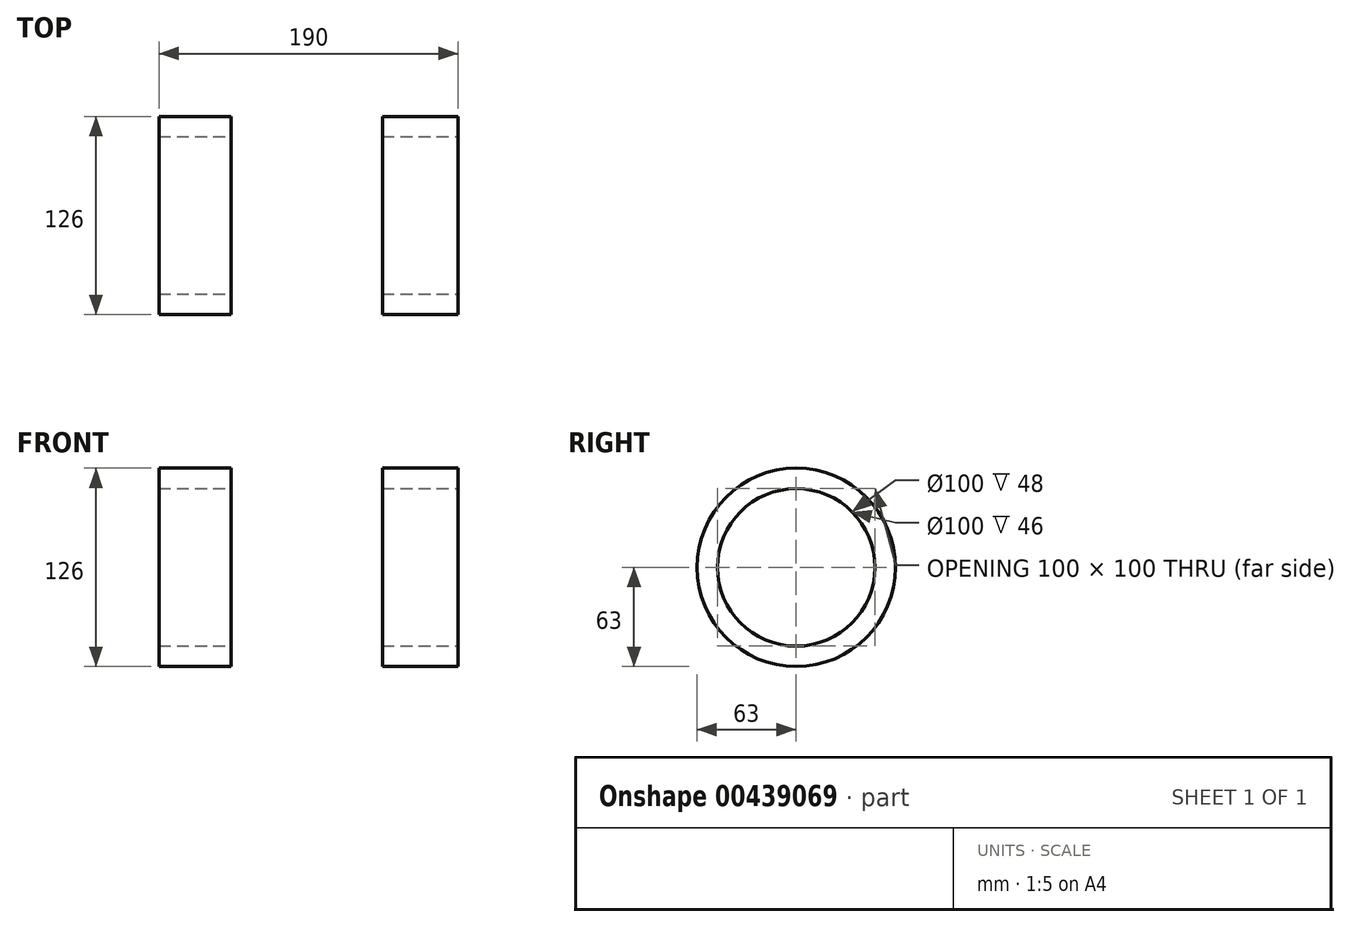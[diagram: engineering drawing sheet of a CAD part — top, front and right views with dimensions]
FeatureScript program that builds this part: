
annotation { "Feature Type Name" : "Feature", "Feature Type Description" : "" }
export const myFeature = defineFeature(function(context is Context, id is Id, definition is map)
    precondition{}
    {
        {
            var Q0;
            Q0=qCreatedBy(makeId("Right.planeOp"),FACE);
            var sketch = newSketch(context, id + "F0", { "sketchPlane" : qUnion([Q0])});
            skCircle(sketch, "E0", {"center": v(0, 0) * mm, "radius": 63 * mm});
            skSolve(sketch);
        }
        {
            var Q0;
            Q0=qSketchRegion(id+"F0",true);
            extrude(context, id + "F1", {"entities" : qUnion([Q0]), "depth" : 190 * mm});
        }
        {
            var Q0;
            Q0=makeQuery(id+"F1.opExtrude","CAP_FACE",FACE,{"disambiguationData":[OSD([sQuery(id+"F0.wireOp",EDGE,"E0")])],"isStart":false});
            var sketch = newSketch(context, id + "F2", { "sketchPlane" : qUnion([Q0])});
            skCircle(sketch, "E1", {"center": v(0, 0) * mm, "radius": 50 * mm});
            skSolve(sketch);
        }
        {
            var Q0;
            Q0=qSketchRegion(id+"F2",true);
            extrude(context, id + "F3", {"entities" : qUnion([Q0]), "operationType" : NewBodyOperationType.REMOVE, "oppositeDirection" : true, "depth" : 190 * mm});
        }
        {
            var Q0;
            Q0=qCreatedBy(makeId("Front.planeOp"),FACE);
            var sketch = newSketch(context, id + "F4", { "sketchPlane" : qUnion([Q0])});
            skLineSegment(sketch, "E2.bottom", {"start": v(46, 63) * mm, "end": v(142, 63) * mm});
            skLineSegment(sketch, "E2.top", {"start": v(46, -63) * mm, "end": v(142, -63) * mm});
            skLineSegment(sketch, "E2.left", {"start": v(46, 63) * mm, "end": v(46, -63) * mm});
            skLineSegment(sketch, "E2.right", {"start": v(142, 63) * mm, "end": v(142, -63) * mm});
            skSolve(sketch);
        }
        {
            var Q0;
            Q0=qSketchRegion(id+"F4",true);
            extrude(context, id + "F5", {"entities" : qUnion([Q0]), "operationType" : NewBodyOperationType.REMOVE, "oppositeDirection" : true, "depth" : 70 * mm, "hasSecondDirection" : true, "secondDirectionOppositeDirection" : false, "secondDirectionDepth" : 70 * mm});
        }
    });
